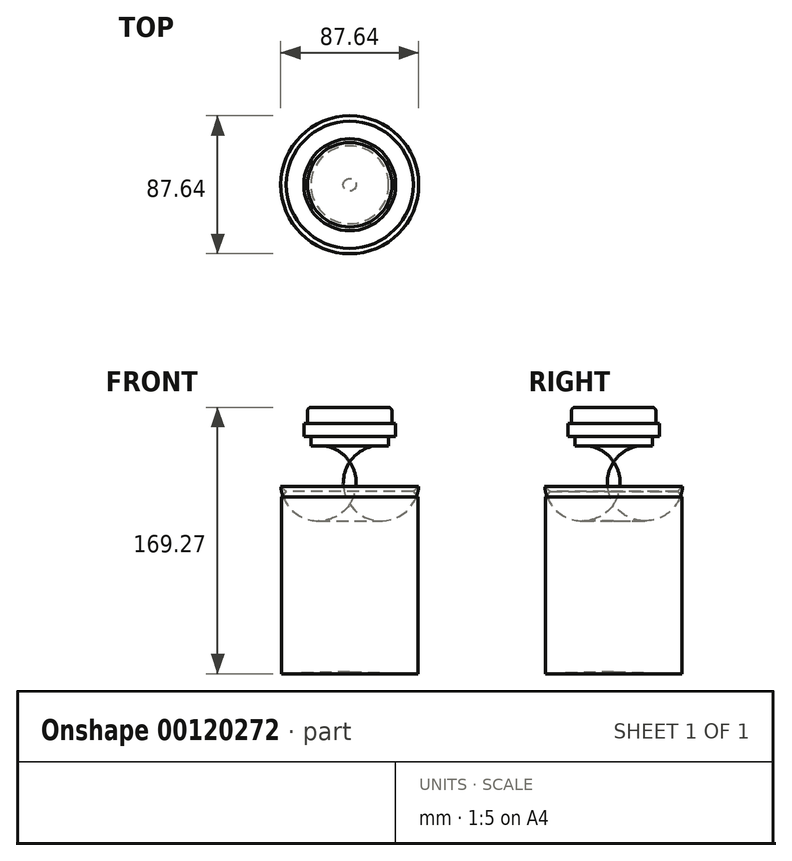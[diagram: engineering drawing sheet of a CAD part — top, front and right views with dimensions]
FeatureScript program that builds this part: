
annotation { "Feature Type Name" : "Feature", "Feature Type Description" : "" }
export const myFeature = defineFeature(function(context is Context, id is Id, definition is map)
    precondition{}
    {
        {
            var Q0;
            Q0=qCreatedBy(makeId("Front.planeOp"),FACE);
            var sketch = newSketch(context, id + "F0", { "sketchPlane" : qUnion([Q0])});
            skLineSegment(sketch, "E0", {"start": v(0, 63.02) * mm, "end": v(26.82, 63.02) * mm});
            skLineSegment(sketch, "E1", {"start": v(26.82, 63.02) * mm, "end": v(26.82, 52.6) * mm});
            skLineSegment(sketch, "E2", {"start": v(26.82, 52.6) * mm, "end": v(29.2, 52.6) * mm});
            skLineSegment(sketch, "E3", {"start": v(29.2, 52.6) * mm, "end": v(29.2, 50.21) * mm});
            skLineSegment(sketch, "E4", {"start": v(29.2, 50.21) * mm, "end": v(29.2, 44.55) * mm});
            skLineSegment(sketch, "E5", {"start": v(29.2, 44.55) * mm, "end": v(24.73, 44.55) * mm});
            skLineSegment(sketch, "E6", {"start": v(24.73, 44.55) * mm, "end": v(24.73, 38.38) * mm});
            skArc(sketch, "E7", {"start": v(43.82, 12.63) * mm, "mid": v(39.2, 29.16) * mm, "end": v(24.73, 38.38) * mm});
            skLineSegment(sketch, "E8", {"start": v(43.82, 12.63) * mm, "end": v(40.36, 9.55) * mm});
            skLineSegment(sketch, "E9", {"start": v(40.36, 9.55) * mm, "end": v(43.49, 6.04) * mm});
            skLineSegment(sketch, "E10", {"start": v(43.49, 6.04) * mm, "end": v(43.49, -106.25) * mm});
            skLineSegment(sketch, "E11", {"start": v(0, 63.02) * mm, "end": v(0, -104.95) * mm});
            skLineSegment(sketch, "E12", {"start": v(0, -104.95) * mm, "end": v(43.49, -106.25) * mm});
            skSolve(sketch);
        }
        {
            var Q0;
            Q0 = qSketchRegion(id + "F0", true);
            var Q1;
            Q1=sQuery(id+"F0.wireOp",EDGE,"E11");
            revolve(context, id + "F1", {"entities" : qUnion([Q0]), "axis" : qUnion([Q1]), "revolveType" : RevolveType.FULL});
        }
        {
            var Q0;
            Q0=makeQuery(id+"F1.opRevolve","SWEPT_EDGE",EDGE,{"disambiguationData":[OSD([sQuery(id+"F0.wireOp",EDGE,"E0"),sQuery(id+"F0.wireOp",EDGE,"E1")])]});
            fillet(context, id + "F2", {"entities" : qUnion([Q0]), "radius" : 2.54 * mm, "tangentPropagation" : true, "allowEdgeOverflow" : false});
        }
    });
